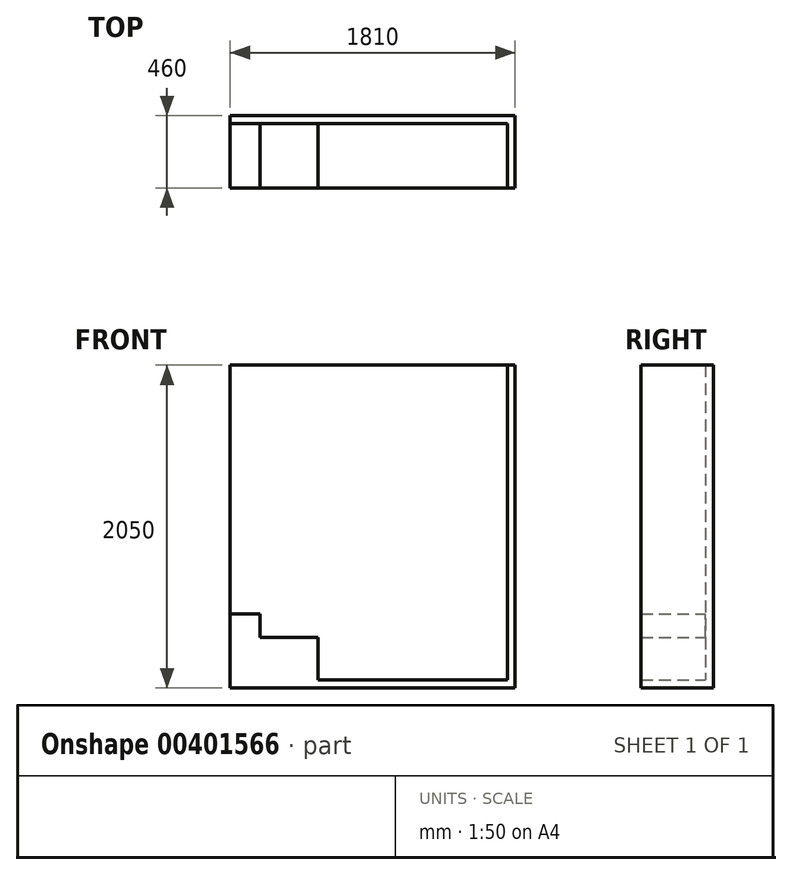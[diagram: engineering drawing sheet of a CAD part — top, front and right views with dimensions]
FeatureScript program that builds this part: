
annotation { "Feature Type Name" : "Feature", "Feature Type Description" : "" }
export const myFeature = defineFeature(function(context is Context, id is Id, definition is map)
    precondition{}
    {
        {
            var Q0;
            Q0=qCreatedBy(makeId("Front.planeOp"),FACE);
            var sketch = newSketch(context, id + "F0", { "sketchPlane" : qUnion([Q0])});
            skLineSegment(sketch, "E0.bottom", {"start": v(-2223.85, 0) * mm, "end": v(-2413.85, 0) * mm});
            skLineSegment(sketch, "E0.top", {"start": v(-2223.85, 420) * mm, "end": v(-2413.85, 420) * mm});
            skLineSegment(sketch, "E0.left", {"start": v(-2223.85, 0) * mm, "end": v(-2223.85, 420) * mm});
            skLineSegment(sketch, "E0.right", {"start": v(-2413.85, 0) * mm, "end": v(-2413.85, 420) * mm});
            skLineSegment(sketch, "E1.bottom", {"start": v(-2223.85, 270) * mm, "end": v(-1853.85, 270) * mm});
            skLineSegment(sketch, "E1.top", {"start": v(-2223.85, 0) * mm, "end": v(-1853.85, 0) * mm});
            skLineSegment(sketch, "E1.left", {"start": v(-2223.85, 270) * mm, "end": v(-2223.85, 0) * mm});
            skLineSegment(sketch, "E1.right", {"start": v(-1853.85, 270) * mm, "end": v(-1853.85, 0) * mm});
            skLineSegment(sketch, "E2.bottom", {"start": v(-653.85, 2000) * mm, "end": v(-603.85, 2000) * mm});
            skLineSegment(sketch, "E2.top", {"start": v(-653.85, 0) * mm, "end": v(-603.85, 0) * mm});
            skLineSegment(sketch, "E2.left", {"start": v(-653.85, 2000) * mm, "end": v(-653.85, 0) * mm});
            skLineSegment(sketch, "E2.right", {"start": v(-603.85, 2000) * mm, "end": v(-603.85, 0) * mm});
            skLineSegment(sketch, "E3.bottom", {"start": v(-603.85, 0) * mm, "end": v(-2413.85, 0) * mm});
            skLineSegment(sketch, "E3.top", {"start": v(-603.85, -50) * mm, "end": v(-2413.85, -50) * mm});
            skLineSegment(sketch, "E3.left", {"start": v(-603.85, 0) * mm, "end": v(-603.85, -50) * mm});
            skLineSegment(sketch, "E3.right", {"start": v(-2413.85, 0) * mm, "end": v(-2413.85, -50) * mm});
            skSolve(sketch);
        }
        {
            var Q0;
            Q0 = qSketchRegion(id + "F0", true);
            extrude(context, id + "F1", {"entities" : qUnion([Q0]), "depth" : 410 * mm});
        }
        {
            var Q0;
            Q0=makeQuery(id+"F1.opExtrude","CAP_FACE",FACE,{"disambiguationData":[OSD([sQuery(id+"F0.wireOp",EDGE,"E0.top"),sQuery(id+"F0.wireOp",EDGE,"E0.left"),sQuery(id+"F0.wireOp",EDGE,"E0.right"),sQuery(id+"F0.wireOp",EDGE,"E1.bottom"),sQuery(id+"F0.wireOp",EDGE,"E1.right"),sQuery(id+"F0.wireOp",EDGE,"E2.bottom"),sQuery(id+"F0.wireOp",EDGE,"E2.left"),sQuery(id+"F0.wireOp",EDGE,"E2.right"),sQuery(id+"F0.wireOp",EDGE,"E3.bottom"),sQuery(id+"F0.wireOp",EDGE,"E3.top"),sQuery(id+"F0.wireOp",EDGE,"E3.left"),sQuery(id+"F0.wireOp",EDGE,"E3.right")])],"isStart":true});
            var sketch = newSketch(context, id + "F2", { "sketchPlane" : qUnion([Q0])});
            skLineSegment(sketch, "E4.bottom", {"start": v(603.85, 2000) * mm, "end": v(2413.85, 2000) * mm});
            skLineSegment(sketch, "E4.top", {"start": v(603.85, -50) * mm, "end": v(2413.85, -50) * mm});
            skLineSegment(sketch, "E4.left", {"start": v(603.85, 2000) * mm, "end": v(603.85, -50) * mm});
            skLineSegment(sketch, "E4.right", {"start": v(2413.85, 2000) * mm, "end": v(2413.85, -50) * mm});
            skSolve(sketch);
        }
        {
            var Q0;
            Q0 = qSketchRegion(id + "F2", true);
            extrude(context, id + "F3", {"entities" : qUnion([Q0]), "operationType" : NewBodyOperationType.ADD, "depth" : 50 * mm});
        }
    });
